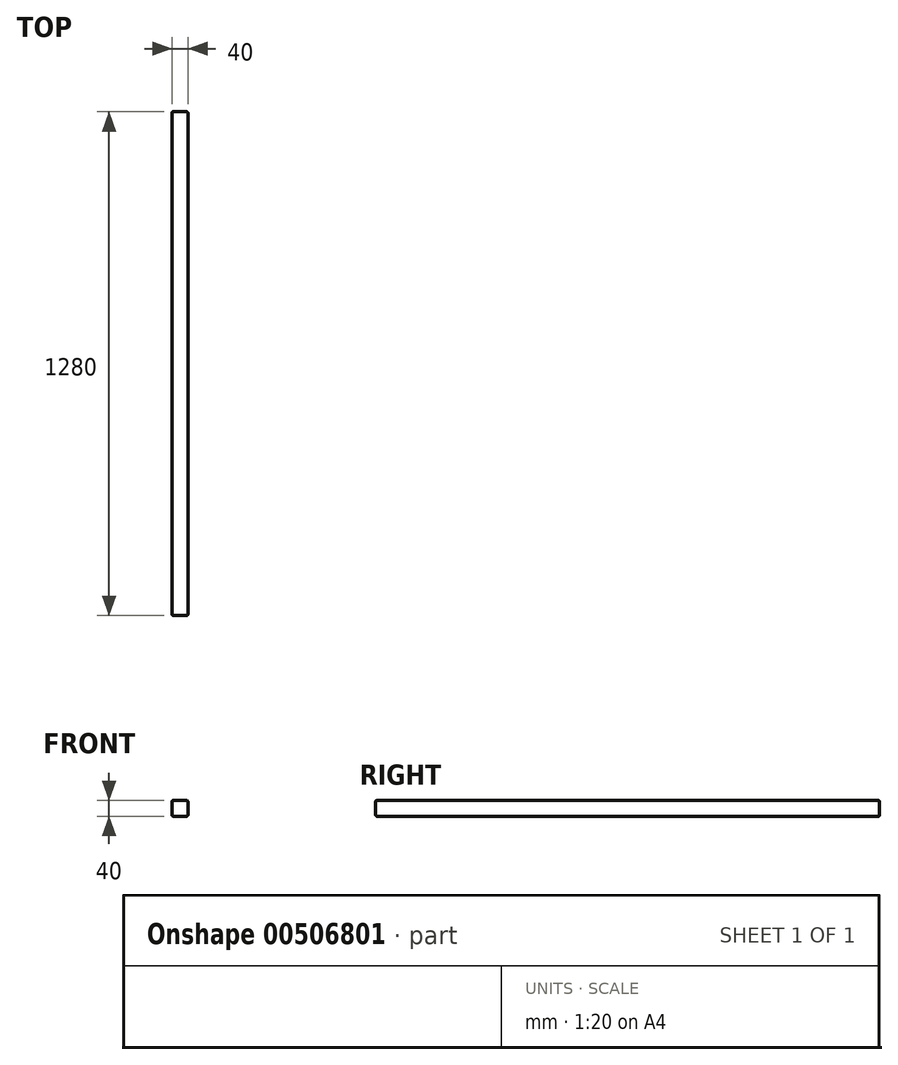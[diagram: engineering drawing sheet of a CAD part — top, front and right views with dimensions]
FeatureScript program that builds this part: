
annotation { "Feature Type Name" : "Feature", "Feature Type Description" : "" }
export const myFeature = defineFeature(function(context is Context, id is Id, definition is map)
    precondition{}
    {
        {
            var Q0;
            Q0=qCreatedBy(makeId("Front.planeOp"),FACE);
            var sketch = newSketch(context, id + "F0", { "sketchPlane" : qUnion([Q0])});
            skLineSegment(sketch, "E0.bottom", {"start": v(-162.58, 40) * mm, "end": v(-122.58, 40) * mm});
            skLineSegment(sketch, "E0.top", {"start": v(-162.58, 0) * mm, "end": v(-122.58, 0) * mm});
            skLineSegment(sketch, "E0.left", {"start": v(-162.58, 40) * mm, "end": v(-162.58, 0) * mm});
            skLineSegment(sketch, "E0.right", {"start": v(-122.58, 40) * mm, "end": v(-122.58, 0) * mm});
            skSolve(sketch);
        }
        {
            var Q0;
            Q0=makeQuery(id+"F0.imprint","IMPRINT",FACE,{"disambiguationData":[TD([[makeQuery(id+"F0.imprint","IMPRINT",EDGE,{"derivedFrom":sQuery(id+"F0.wireOp",EDGE,"E0.bottom")}),-1.0]])]});
            extrude(context, id + "F1", {"entities" : qUnion([Q0]), "depth" : 1280 * mm});
        }
        {
            var Q0;
            Q0=makeQuery(id+"F1.opExtrude","SWEPT_FACE",FACE,{"disambiguationData":[OSD([sQuery(id+"F0.wireOp",EDGE,"E0.right")])]});
            var Q1;
            Q1=makeQuery(id+"F1.opExtrude","SWEPT_EDGE",EDGE,{"disambiguationData":[OSD([sQuery(id+"F0.wireOp",EDGE,"E0.bottom"),sQuery(id+"F0.wireOp",EDGE,"E0.right")])]});
            var Q2;
            Q2=makeQuery(id+"F1.opExtrude","SWEPT_FACE",FACE,{"disambiguationData":[OSD([sQuery(id+"F0.wireOp",EDGE,"E0.top")])]});
            var Q3;
            Q3=makeQuery(id+"F1.opExtrude","SWEPT_FACE",FACE,{"disambiguationData":[OSD([sQuery(id+"F0.wireOp",EDGE,"E0.left")])]});
            var Q4;
            Q4=makeQuery(id+"F1.opExtrude","SWEPT_FACE",FACE,{"disambiguationData":[OSD([sQuery(id+"F0.wireOp",EDGE,"E0.bottom")])]});
            fillet(context, id + "F2", {"entities" : qUnion([Q0, Q1, Q2, Q3, Q4]), "radius" : 3 * mm, "tangentPropagation" : true, "allowEdgeOverflow" : false});
        }
        {
            var Q0;
            Q0=makeQuery(id+"F1.opExtrude","SWEPT_FACE",FACE,{"disambiguationData":[OSD([sQuery(id+"F0.wireOp",EDGE,"E0.right")])]});
            var sketch = newSketch(context, id + "F3", { "sketchPlane" : qUnion([Q0])});
            skLineSegment(sketch, "E1", {"start": v(-1277, 20) * mm, "end": v(-1260, 20) * mm});
            skLineSegment(sketch, "E2", {"start": v(-1260, 20) * mm, "end": v(-1010, 20) * mm});
            skLineSegment(sketch, "E3", {"start": v(-1010, 20) * mm, "end": v(-271, 20) * mm});
            skLineSegment(sketch, "E4", {"start": v(-271, 20) * mm, "end": v(-21, 20) * mm});
            skLineSegment(sketch, "E5", {"start": v(-21, 20) * mm, "end": v(-3, 20) * mm});
            skSolve(sketch);
        }
    });
